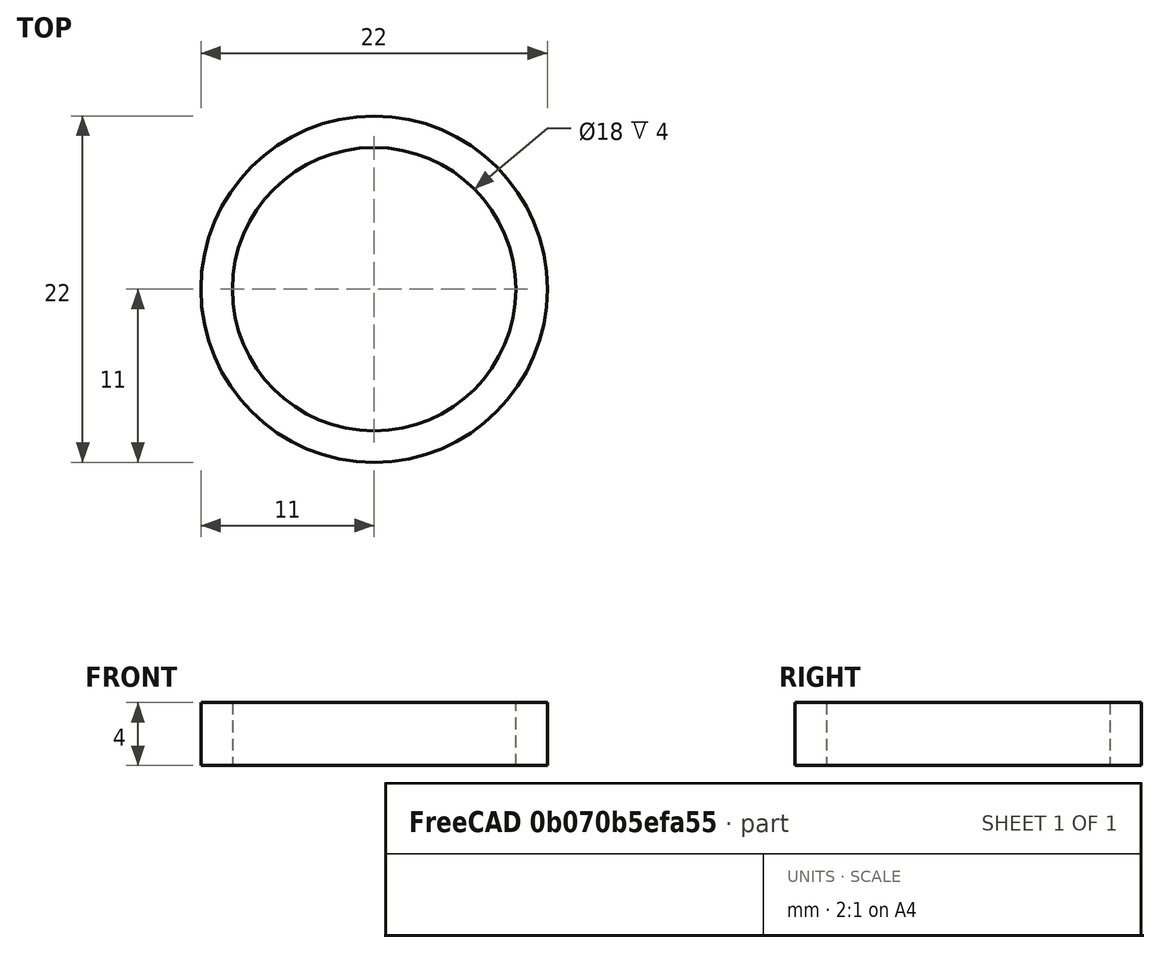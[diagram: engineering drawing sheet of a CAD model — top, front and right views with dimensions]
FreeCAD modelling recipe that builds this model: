
FCSTD DOCUMENT  (FreeCAD 0.18R16110 (Git))
Label: pumpnosletest
License: All rights reserved
LicenseURL: http://en.wikipedia.org/wiki/All_rights_reserved
objects: Sketcher::SketchObject×1, PartDesign::Pad×1, PartDesign::Body×1
note: 4 computed .brp shape members not serialized (recipe doc carries the construction recipe); baked Part::Feature solids carry a one-line shape summary decoded from their .brp

FEATURE [Sketcher::SketchObject] Sketch
  MapMode = 5
  Support = -> [XY_Plane]
  sketch-geometry (2):
    g0: Circle CenterX=0 CenterY=0 CenterZ=0 NormalX=0 NormalY=0 NormalZ=1 AngleXU=0 Radius=9
    g1: Circle CenterX=0 CenterY=0 CenterZ=0 NormalX=0 NormalY=0 NormalZ=1 AngleXU=0 Radius=11
  constraints (4):
    c: Coincident(g0,g-1)
    c: Coincident(g1,g0)
    c: Radius(g0) = 9
    c: Radius(g1) = 11
FEATURE [PartDesign::Pad] Pad
  Length = 4
  Length2 = 100
  Profile = -> Sketch
  Type = 0
FEATURE [PartDesign::Body] Body
  Group = -> [Sketch,Pad]
  Origin = -> Origin
  Tip = -> Pad
